# Revit family: tc
name_source: partatom
category: Pipe Fittings
revit_build: Autodesk Revit 2018 (Build: 20170223_1515(x64)
units: mm (PartAtom-declared; Revit-internal decimal feet)

## family parameters
Always vertical = Yes
Cut with Voids When Loaded = No
OmniClass Number = 23.27.43.00
Part Type = Elbow
Round Connector Dimension = Use Diameter
Shared = No
Work Plane-Based = No

## types (1)
- 90130-80-110-168
    Assembly Code = D2040100
    BIMobject category = Joints
    Description = Elbow Conector
    Design country = Italy
    Edition number = 1
    IFC Classification = Pipe Fitting
    Keynote = 15410
    Lookup Table Name = 90130_80-110-168
    Manufacturer = Aignep Spa
    Manufacturer country = Italy
    Manufacturer name = Aignep Spa
    Material main = Aluminium
    Model = 90130-80-110-168
    OmniClass Code = 23-27 43 00
    OmniClass Description = Pipe Fittings
    Product Guid = f8e249cf-ef4c-4725-8d01-a2e5ac593bd8
    Product Material = AIGNEP - Brass - Yellow
    Product SKU = Elbow-Connector-90130-80-110-168
    Product certification = https://www.aignep.com
    Product data url = https://www.bimobject.com
    Product family = INFINITY
    Product group = Fittings
    Product name = Elbow Connector 90130
    Product url = https://www.aignep.com
    QR code = https://www.bimobject.com
    URL = https://www.aignep.com

## geometry (parser evidence)
native form markers: Sweep x3
no freeform markers — native parametric forms only
